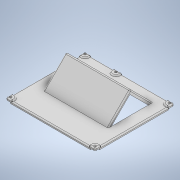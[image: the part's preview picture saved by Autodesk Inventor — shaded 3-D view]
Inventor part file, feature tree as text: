
AUTODESK INVENTOR PART (.ipt)
format: ipt  version: 2020 (Build 240168000, 168)  size: 425,472 bytes
history: native  units: in
note: dims shown in document units (in); Inventor stores cm internally (conversion verified against a paired STEP export)
features: extrude x10, sketch x10, fillet x5, chamfer x1
ambient origin geometry x8: Origin, YZ Plane, XZ Plane, XY Plane, X Axis, Y Axis, Z Axis, Center Point
bodies: Solid1 (feature_tree)
feature tree (26):
  extrude  "Extrusion1"  Depth=5.5118in
  extrude  "Extrusion2"  Depth=0.1575in
  extrude  "Extrusion6"  Depth=0.1575in
  chamfer  "Chamfer1"  Distance=0.2362in
  extrude  "Extrusion7"  Depth=2.2047in
  extrude  "Extrusion8"  Depth=0.0787in TaperAngle=45.0deg
  extrude  "Extrusion9"  Depth=0.1575in
  extrude  "Extrusion10"  Depth=0.1575in
  extrude  "Extrusion11"  Depth=0.0787in
  extrude  "Extrusion12"  Depth=0.0787in
  extrude  "Extrusion13"  Depth=0.0787in
  fillet  "Fillet1"  Radius=0.3937in
  fillet  "Fillet2"  Radius=0.1575in
  fillet  "Fillet3"  Radius=2.0276in
  fillet  "Fillet4"  Radius=0.5118in
  fillet  "Fillet5"  Radius=0.0787in
  sketch  "Sketch1"  dims[d0=6.2151in d1=5.5118in]
  sketch  "Sketch2"  dims[d2=0.1575in d3=0.0in d4=0.1575in]
  sketch  "Sketch6"  dims[d5=0.1575in d6=0.1575in]
  sketch  "Sketch7"  dims[d7=0.1575in]
  sketch  "Sketch8"  dims[d8=0.1575in d9=0.2362in d10=0.0in]
  sketch  "Sketch9"  dims[d24=4.5276in d25=2.2047in]
  sketch  "Sketch10"  dims[d26=0.2362in d27=0.0in d28=0.1575in d29=0.0787in d30=45.0deg]
  sketch  "Sketch11"  dims[d31=2.2047in d32=0.0in d33=0.1575in]
  sketch  "Sketch12"  dims[d34=0.1575in d35=0.1575in]
  sketch  "Sketch13"  dims[d36=0.1575in d37=3.0906in d38=0.315in d39=0.315in d40=0.3937in d41=0.0in d42=0.1575in d43=2.0276in d44=0.0in d45=0.5118in d46=0.0in d47=0.0787in d48=0.0in d49=0.0866in d50=0.1614in d51=0.0in d52=0.5906in d53=0.5906in d54=0.5906in d55=0.5906in d56=0.5906in d57=0.0787in d58=0.0in d59=0.0787in d60=0.0787in d61=0.0787in d62=0.0787in d63=0.0787in]
